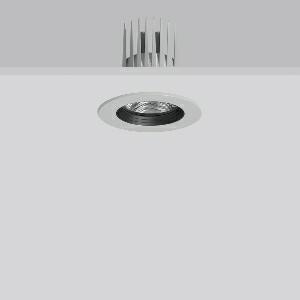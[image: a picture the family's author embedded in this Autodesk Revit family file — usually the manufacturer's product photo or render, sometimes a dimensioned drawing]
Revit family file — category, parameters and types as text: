
# Revit family: heledon_mini_e_901749_004_3_a654
name_source: partatom
category: Lighting Fixtures
units: mm (PartAtom-declared; Revit-internal decimal feet)

## family parameters
Cut with Voids When Loaded = No
Host = Face
Light Source = No
Part Type = Normal
Room Calculation Point = No
Round Connector Dimension = Use Diameter
Shared = No

## types (1)
- HELEDON mini E (1 x LED Modul 935, 3600 lm, 3500)
    Apparent Load = 29 VA
    Approval mark = CE
    CIE Flux Codes = 99 100 100 100 100
    Color Rendering = 92
    Color Temperature = 3500
    Default Elevation = 1800 mm
    Description = Series: HELEDON mini
Round recessed downlight. Housing: die-cast aluminium, powder-coated. Black plastic ring and recessed LED to prevent glare from the side. Optical assembly with reflector made of MIRO-Silver with 98% total light reflection for outstanding efficiency - can be changed without tools. Best colour rendering index Ra>90. Suitable for Recessed ceiling mounting. Installation without tools thanks to spring fastening system. Including separate LED converter with connecting cable 600 mm.High quality converter without flickering and stroboscopic effect. Through-wiring box (5 pole) available as accessory. The following accessories can be mounted without use of tools: interchangeable lenses, decorative glasses, honeycomb louvre, clear and frosted diffusers, white interchangeable plastic ring. 
Colour: silver
Diameter: 124 mm
Height: 3 mm
Cut-out diameter: 114 mm
Recess height: 170 mm
Luminaire: recess height: 120 mm
Lamp: LED
Socket: without socket
Colour temperature: 3500K
Colour rendering index (CRI): 92
System power: 29 W
Rated luminous flux: 3600 lm
Luminous efficiency: 124 lm/W
Control gear: Regulated power supply
Protection class: II
Type of protection: IP 20
    Height = 0 mm  [stored 0 ft]
    Lamp = 1 x LED Modul 935
    Lamp Light Flux = 3600 lm
    Lamp count = 1
    Length = 124 mm  [stored 0.406824 ft]
    Lifetime = 50000 h
    Luminous efficacy = 124 lm/W
    Manufacturer = RZB
    ModVariant = No
    Model = 901749.004.3
    Mounting Place = Ceiling
    Mounting Type = Recessed
    Number of Poles = 1
    OnlyDefault = Yes
    Power Factor = 1
    Product Name = HELEDON mini E
    Product group = Recessed downlights
    ProductGroupID = 402
    Protection Class = Protection class II
    Protection Degree = IP 20
    RLX_Detail_Level = 1
    RLX_Emergency_Light_Flux = 0 lm
    RLX_Emergency_Type = 0
    RLX_Emergency_Type_DB = No
    RlxData = <blob elided: 127625 chars, md5=58fbac6b>
    Socket = socket
    Standby Power = 0 W
    System Light Flux = 3600 lm
    System Power = 29 W
    Type Comments = Product without accessories
    Type Image = 901657.004.jpg
    URL = http://relux.com
    VarID = ---
    Voltage = 230 V
    Voltage Range = 220-240 V
    Weight = 0.00 kg
    Width = 0 mm  [stored 0 ft]

note: [stored X ft] marks values corroborated as IEEE doubles in the binary element streams (Revit-internal decimal feet)

## geometry (parser evidence)
native form markers: Blend x4, Sweep x12
no freeform markers — native parametric forms only
